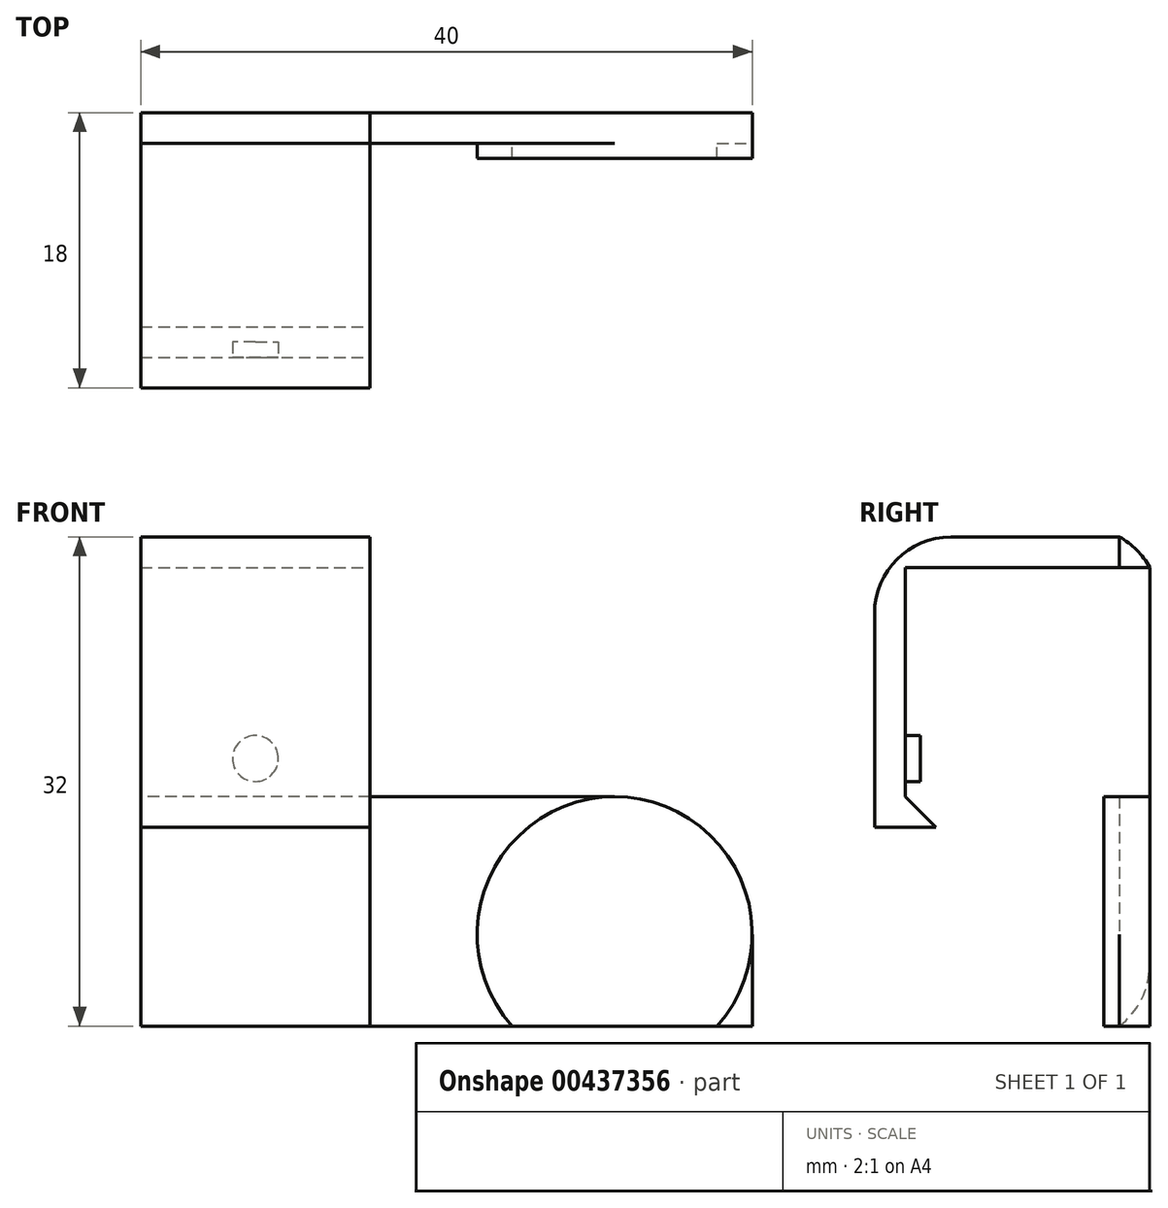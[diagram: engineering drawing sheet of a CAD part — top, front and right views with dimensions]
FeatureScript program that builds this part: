
annotation { "Feature Type Name" : "Feature", "Feature Type Description" : "" }
export const myFeature = defineFeature(function(context is Context, id is Id, definition is map)
    precondition{}
    {
        {
            var Q0;
            Q0=qCreatedBy(makeId("Top.planeOp"),FACE);
            var sketch = newSketch(context, id + "F0", { "sketchPlane" : qUnion([Q0])});
            skLineSegment(sketch, "E0.bottom", {"start": v(0, 0) * mm, "end": v(40, 0) * mm});
            skLineSegment(sketch, "E0.top", {"start": v(0, -2) * mm, "end": v(40, -2) * mm});
            skLineSegment(sketch, "E0.left", {"start": v(0, 0) * mm, "end": v(0, -2) * mm});
            skLineSegment(sketch, "E0.right", {"start": v(40, 0) * mm, "end": v(40, -2) * mm});
            skSolve(sketch);
        }
        {
            var Q0;
            Q0=makeQuery(id+"F0.imprint","IMPRINT",FACE,{"disambiguationData":[TD([[makeQuery(id+"F0.imprint","IMPRINT",EDGE,{"derivedFrom":sQuery(id+"F0.wireOp",EDGE,"E0.bottom")}),-1.0]])]});
            extrude(context, id + "F1", {"entities" : qUnion([Q0]), "depth" : 15 * mm});
        }
        {
            var Q0;
            Q0=qCreatedBy(makeId("Top.planeOp"),FACE);
            var sketch = newSketch(context, id + "F2", { "sketchPlane" : qUnion([Q0])});
            skLineSegment(sketch, "E1.bottom", {"start": v(0, 0) * mm, "end": v(15, 0) * mm});
            skLineSegment(sketch, "E1.top", {"start": v(0, -2) * mm, "end": v(15, -2) * mm});
            skLineSegment(sketch, "E1.left", {"start": v(0, 0) * mm, "end": v(0, -2) * mm});
            skLineSegment(sketch, "E1.right", {"start": v(15, 0) * mm, "end": v(15, -2) * mm});
            skSolve(sketch);
        }
        {
            var Q0;
            Q0 = qSketchRegion(id + "F2", true);
            extrude(context, id + "F3", {"entities" : qUnion([Q0]), "depth" : 30 * mm});
        }
        {
            var Q0;
            Q0=makeQuery(id+"F3.opExtrude","CAP_FACE",FACE,{"disambiguationData":[OSD([sQuery(id+"F2.wireOp",EDGE,"E1.bottom"),sQuery(id+"F2.wireOp",EDGE,"E1.top"),sQuery(id+"F2.wireOp",EDGE,"E1.left"),sQuery(id+"F2.wireOp",EDGE,"E1.right")])],"isStart":false});
            var sketch = newSketch(context, id + "F4", { "sketchPlane" : qUnion([Q0])});
            skLineSegment(sketch, "E2.bottom", {"start": v(0, 0) * mm, "end": v(15, 0) * mm});
            skLineSegment(sketch, "E2.top", {"start": v(0, -18) * mm, "end": v(15, -18) * mm});
            skLineSegment(sketch, "E2.left", {"start": v(0, 0) * mm, "end": v(0, -18) * mm});
            skLineSegment(sketch, "E2.right", {"start": v(15, 0) * mm, "end": v(15, -18) * mm});
            skSolve(sketch);
        }
        {
            var Q0;
            {var subQ0=sQuery(id+"F4.wireOp",EDGE,"E2.top");Q0=makeQuery(id+"F4.imprint","IMPRINT",FACE,{"disambiguationData":[TD([[makeQuery(id+"F4.imprint","IMPRINT",EDGE,{"derivedFrom":subQ0}),1.0]])]});}
            extrude(context, id + "F5", {"entities" : qUnion([Q0]), "depth" : 2 * mm});
        }
        {
            var Q0;
            {var subQ0=sQuery(id+"F4.wireOp",EDGE,"E2.bottom");Q0=makeQuery(id+"F4.imprint","IMPRINT",FACE,{"disambiguationData":[TD([[makeQuery(id+"F4.imprint","IMPRINT",EDGE,{"derivedFrom":subQ0}),-1.0]])]});}
            extrude(context, id + "F6", {"entities" : qUnion([Q0]), "depth" : 2 * mm});
        }
        {
            var Q0;
            {var subQ0=sQuery(id+"F4.wireOp",EDGE,"E2.top");Q0=makeQuery(id+"F4.imprint","IMPRINT",FACE,{"disambiguationData":[TD([[makeQuery(id+"F4.imprint","IMPRINT",EDGE,{"derivedFrom":subQ0}),1.0]])]});}
            var sketch = newSketch(context, id + "F7", { "sketchPlane" : qUnion([Q0])});
            skLineSegment(sketch, "E3.bottom", {"start": v(0, -18) * mm, "end": v(15, -18) * mm});
            skLineSegment(sketch, "E3.top", {"start": v(0, -16) * mm, "end": v(15, -16) * mm});
            skLineSegment(sketch, "E3.left", {"start": v(0, -18) * mm, "end": v(0, -16) * mm});
            skLineSegment(sketch, "E3.right", {"start": v(15, -18) * mm, "end": v(15, -16) * mm});
            skSolve(sketch);
        }
        {
            var Q0;
            Q0=makeQuery(id+"F7.imprint","IMPRINT",FACE,{"disambiguationData":[TD([[makeQuery(id+"F7.imprint","IMPRINT",EDGE,{"derivedFrom":sQuery(id+"F7.wireOp",EDGE,"E3.bottom")}),1.0]])]});
            extrude(context, id + "F8", {"entities" : qUnion([Q0]), "operationType" : NewBodyOperationType.ADD, "oppositeDirection" : true, "depth" : 17 * mm});
        }
        {
            var Q0;
            Q0=makeQuery(id+"F5.opExtrude","CAP_EDGE",EDGE,{"disambiguationData":[OSD([sQuery(id+"F4.wireOp",EDGE,"E2.top")])],"isStart":false});
            fillet(context, id + "F9", {"entities" : qUnion([Q0]), "radius" : 5 * mm, "tangentPropagation" : true, "allowEdgeOverflow" : false});
        }
        {
            var Q0;
            Q0=makeQuery(id+"F3.opExtrude","CAP_EDGE",EDGE,{"disambiguationData":[OSD([sQuery(id+"F2.wireOp",EDGE,"E1.bottom")])],"isStart":true});
            fillet(context, id + "F10", {"entities" : qUnion([Q0]), "radius" : 5 * mm, "tangentPropagation" : true, "allowEdgeOverflow" : false});
        }
        {
            var Q0;
            Q0=makeQuery(id+"F8.opExtrude","SWEPT_FACE",FACE,{"disambiguationData":[OSD([sQuery(id+"F7.wireOp",EDGE,"E3.top")])]});
            var sketch = newSketch(context, id + "F11", { "sketchPlane" : qUnion([Q0])});
            skLineSegment(sketch, "E4", {"start": v(-7.5, 21) * mm, "end": v(-7.5, 32) * mm});
            skLineSegment(sketch, "E5", {"start": v(-7.5, 21) * mm, "end": v(-7.5, 17.5) * mm});
            skCircle(sketch, "E6", {"center": v(-7.5, 17.5) * mm, "radius": 1.5 * mm});
            skLineSegment(sketch, "E7.bottom", {"start": v(-15, 13) * mm, "end": v(0, 13) * mm});
            skLineSegment(sketch, "E7.top", {"start": v(-15, 15) * mm, "end": v(0, 15) * mm});
            skLineSegment(sketch, "E7.left", {"start": v(-15, 13) * mm, "end": v(-15, 15) * mm});
            skLineSegment(sketch, "E7.right", {"start": v(0, 13) * mm, "end": v(0, 15) * mm});
            skSolve(sketch);
        }
        {
            var Q0;
            Q0=makeQuery(id+"F11.imprint","IMPRINT",FACE,{"disambiguationData":[TD([[makeQuery(id+"F11.imprint","IMPRINT",EDGE,{"derivedFrom":sQuery(id+"F11.wireOp",EDGE,"E6")}),1.0]])]});
            extrude(context, id + "F12", {"entities" : qUnion([Q0]), "operationType" : NewBodyOperationType.ADD, "depth" : 1 * mm});
        }
        {
            var Q0;
            Q0=makeQuery(id+"F1.opExtrude","SWEPT_FACE",FACE,{"disambiguationData":[OSD([sQuery(id+"F0.wireOp",EDGE,"E0.top")])]});
            var sketch = newSketch(context, id + "F13", { "sketchPlane" : qUnion([Q0])});
            skLineSegment(sketch, "E8", {"start": v(24.1, 8.57) * mm, "end": v(36.01, 8.57) * mm});
            skSolve(sketch);
        }
        {
            var Q0;
            {var subQ0=sQuery(id+"F0.wireOp",EDGE,"E0.top");Q0=makeQuery(id+"F13.imprint","IMPRINT",FACE,{"disambiguationData":[TD([[makeQuery(id+"F13.imprint","IMPRINT",EDGE,{"derivedFrom":makeQuery(id+"F1.opExtrude","CAP_EDGE",EDGE,{"disambiguationData":[OSD([subQ0])],"isStart":false})}),-1.0]])]});}
            var sketch = newSketch(context, id + "F14", { "sketchPlane" : qUnion([Q0])});
            skCircle(sketch, "E9", {"center": v(31, 6) * mm, "radius": 9 * mm});
            skSolve(sketch);
        }
        {
            var Q0;
            {var subQ0=sQuery(id+"F14.wireOp",EDGE,"E9");var subQ1=sQuery(id+"F0.wireOp",EDGE,"E0.top");var subQ2=makeQuery(id+"F14.imprint","INTERSECT",VERTEX,{"derivedFrom":[makeQuery(id+"F13.imprint","IMPRINT",EDGE,{"derivedFrom":makeQuery(id+"F1.opExtrude","CAP_EDGE",EDGE,{"disambiguationData":[OSD([subQ1])],"isStart":false})}),subQ0]});Q0=makeQuery(id+"F14.imprint","IMPRINT",FACE,{"disambiguationData":[TD([[makeQuery(id+"F14.imprint","IMPRINT",EDGE,{"disambiguationData":[TD([[subQ2,1.0]])],"derivedFrom":subQ0}),1.0]])]});}
            extrude(context, id + "F15", {"entities" : qUnion([Q0]), "operationType" : NewBodyOperationType.ADD, "depth" : 1 * mm});
        }
        {
            var Q0;
            Q0=makeQuery(id+"F1.opExtrude","CAP_EDGE",EDGE,{"disambiguationData":[OSD([sQuery(id+"F0.wireOp",EDGE,"E0.right")])],"isStart":false});
            fillet(context, id + "F16", {"entities" : qUnion([Q0]), "radius" : 9 * mm, "tangentPropagation" : true, "allowEdgeOverflow" : false});
        }
        {
            var Q0;
            Q0=makeQuery(id+"F6.opExtrude","CAP_EDGE",EDGE,{"disambiguationData":[OSD([sQuery(id+"F4.wireOp",EDGE,"E2.bottom")])],"isStart":false});
            fillet(context, id + "F17", {"entities" : qUnion([Q0]), "radius" : 5 * mm, "tangentPropagation" : true, "rho" : 0.5, "crossSection" : FilletCrossSection.CONIC, "allowEdgeOverflow" : false});
        }
        {
            var Q0;
            Q0=makeQuery(id+"F11.imprint","IMPRINT",FACE,{"disambiguationData":[TD([[makeQuery(id+"F11.imprint","IMPRINT",EDGE,{"derivedFrom":sQuery(id+"F11.wireOp",EDGE,"E7.bottom")}),-1.0]])]});
            extrude(context, id + "F18", {"entities" : qUnion([Q0]), "operationType" : NewBodyOperationType.ADD, "depth" : 2 * mm});
        }
        {
            var Q0;
            Q0=makeQuery(id+"F18.opExtrude","CAP_EDGE",EDGE,{"disambiguationData":[OSD([sQuery(id+"F11.wireOp",EDGE,"E7.top")])],"isStart":false});
            chamfer(context, id + "F19", {"entities" : qUnion([Q0]), "width" : 2 * mm, "tangentPropagation" : true});
        }
    });
